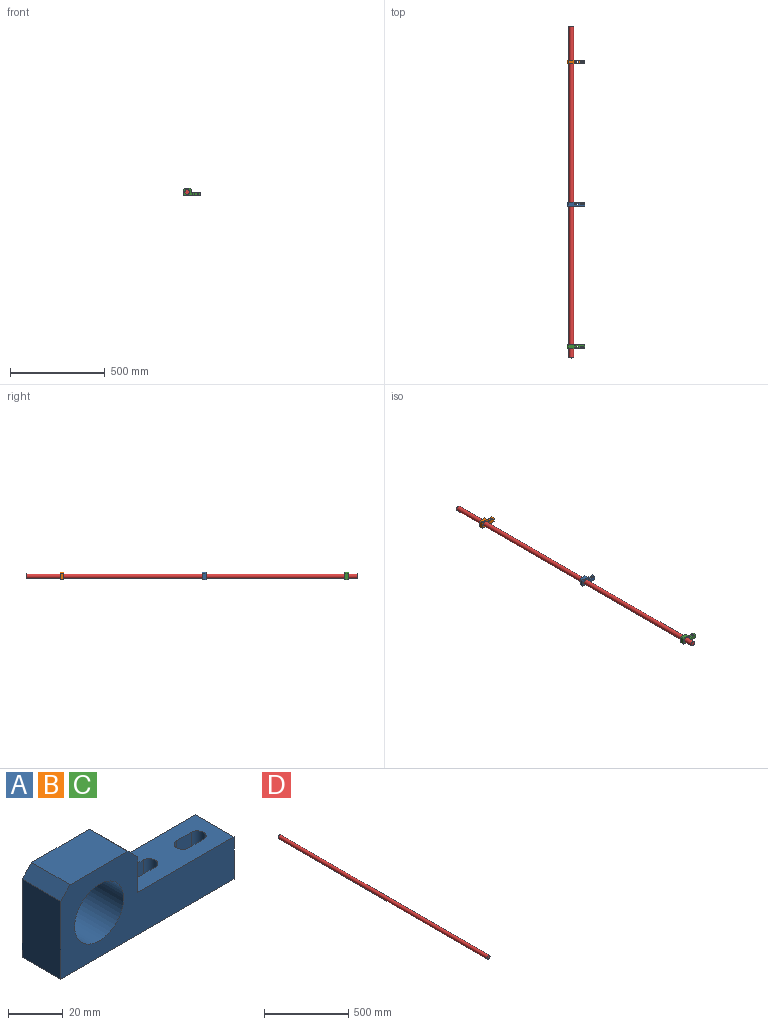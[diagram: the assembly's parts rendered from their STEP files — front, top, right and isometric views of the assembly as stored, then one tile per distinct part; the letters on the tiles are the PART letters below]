
ASSEMBLY  parts=4 mates=2
PART A: 19 faces, bbox 90x20x40 mm
  f0: plane 90x20mm, normal (0,0,-1), area 1640.4mm2, adj f1,f6,f7,f8,f11,f12,f13,f14
  f1: plane 20x19mm, normal (1,0,0), area 380mm2, adj f0,f2,f7,f8
  f2: plane 50x20mm, normal (0,0,1), area 840.4mm2, adj f1,f3,f7,f8,f11,f12,f13,f14
  f3: plane 20x16mm, normal (1,0,0), area 320mm2, adj f2,f7,f8,f10
  f4: plane 30x20mm, normal (0,0,1), area 600mm2, adj f7,f8,f9,f10
  f5: cylinder r=12.7mm len=25.4mm, axis (0,1,0), area 1595.9mm2, adj f7,f8
  f6: plane 35x20mm, normal (-1,0,0), area 700mm2, adj f0,f7,f8,f9
  f7: plane 90x40mm, normal (0,-1,0), area 2018.3mm2, adj f0,f1,f2,f3,f4,f5,f6,f9
  f8: plane 90x40mm, normal (0,1,0), area 2018.3mm2, adj f0,f1,f2,f3,f4,f5,f6,f9
  f9: plane 20x5mm, normal (-0.71,0,0.71), area 141.4mm2, adj f4,f6,f7,f8
  f10: plane 20x5mm, normal (0.71,0,0.71), area 141.4mm2, adj f3,f4,f7,f8
  f11: plane 19x7.69mm, normal (0,1,0), area 146.1mm2, adj f0,f2,f12,f14
  f12: cylinder r=3.15mm len=19mm, axis (0,0,1), area 188.3mm2, adj f0,f2,f11,f13
  f13: plane 19x7.69mm, normal (0,-1,0), area 146.1mm2, adj f0,f2,f12,f14
  f14: cylinder r=3.15mm len=19mm, axis (0,0,1), area 188.3mm2, adj f0,f2,f11,f13
  f15: plane 19x7.69mm, normal (0,1,0), area 146.1mm2, adj f0,f2,f16,f18
  f16: cylinder r=3.15mm len=19mm, axis (0,0,1), area 188.3mm2, adj f0,f2,f15,f17
  f17: plane 19x7.69mm, normal (0,-1,0), area 146.1mm2, adj f0,f2,f16,f18
  f18: cylinder r=3.15mm len=19mm, axis (0,0,1), area 188.3mm2, adj f0,f2,f15,f17
PART B: same geometry as A
PART C: same geometry as A
PART D: 3 faces, bbox 25.4x1750x25.4 mm
  f0: cylinder r=12.7mm len=1750mm, axis (0,1,0), area 139643.8mm2, adj f1,f2
  f1: plane 25.4x25.4mm, normal (0,-1,0), area 506.7mm2, adj f0
  f2: plane 25.4x25.4mm, normal (0,1,0), area 506.7mm2, adj f0
PLACE A t=(-480.02,-472.4,-332.72)mm
PLACE B t=(-480.02,277.6,-332.72)mm
PLACE C t=(-480.02,-1222.4,-332.72)mm
PLACE D t=(-480.02,457.6,-332.72)mm
MATE cylindrical C.f5 <-> D.f0  axis (0,-1,0) through (-480.02,-1242.4,-332.72)mm
MATE planar C.f5 <-> D.f0  axis (0,-1,0) through (-480.02,-1242.4,-332.72)mm
